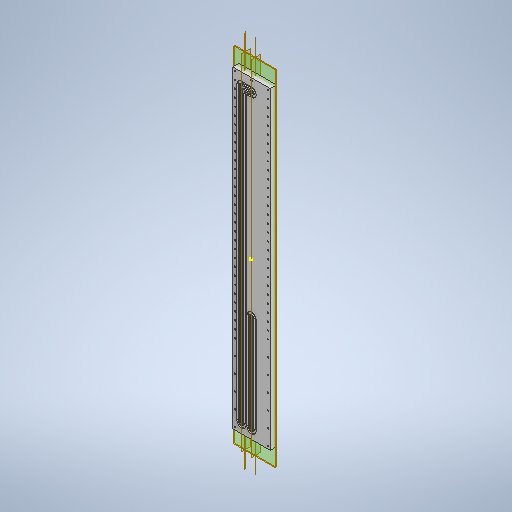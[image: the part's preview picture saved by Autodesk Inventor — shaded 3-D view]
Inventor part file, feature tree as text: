
AUTODESK INVENTOR PART (.ipt)
format: ipt  version: 2025 (Build 290162000, 162)  size: 955,904 bytes
history: native  units: mm
features: sketch x19, hole x11, other x10, extrude x8, pattern_linear x4, plane x4, fillet x1, projected_geometry x1
ambient origin geometry x8: Origin, YZ Plane, XZ Plane, XY Plane, X Axis, Y Axis, Z Axis, Center Point
bodies: Volumenkörper1 (feature_tree)
feature tree (58):
  sketch  "Skizze2"  dims[d3=22.5mm d4=5.0mm]
  sketch  "Skizze1"  dims[d0=90.0deg d1=5.0mm]
  extrude  "Extrusion1"  Depth=5.0mm
  extrude  "Extrusion2"  Depth=5.0mm
  extrude  "Extrusion4"  Depth=35.0mm
  hole  "Bohrung7"  [1 undecoded]
  sketch  "Skizze7"  dims[d14=35.0mm d15=5.0mm]
  hole  "Bohrung10"  [1 undecoded]
  hole  "Bohrung12"  [1 undecoded]
  pattern_linear  "Rechteckige Anordnung5"  Count1=50  [1 undecoded]
  sketch  "Skizze19"  dims[d24=250.0mm d26=10.0mm d27=0.0mm]
  extrude  "Extrusion8"  Depth=30.0mm
  sketch  "Skizze21"  dims[d28=1.6mm d29=0.0mm d68=2.0mm]
  extrude  "Extrusion9"  Depth=10.0mm TaperAngle=0.0deg
  extrude  "Extrusion10"  Depth=2.0mm
  other  "Arbeitsachse2"
  hole  "Bohrung13"  [1 undecoded]
  extrude  "Extrusion11"  TaperAngle=0.0deg  [1 undecoded]
  pattern_linear  "Rechteckige Anordnung6"  Count1=11 Spacing1=49.2mm
  hole  "Bohrung14"  [1 undecoded]
  other  "Arbeitsachse4"
  plane  "Arbeitsebene3"
  plane  "Arbeitsebene5"
  plane  "Arbeitsebene2"
  other  "Arbeitspunkt14"
  other  "Arbeitspunkt11"
  hole  "Bohrung15"  [1 undecoded]
  plane  "Arbeitsebene4"
  other  "Arbeitsachse7"
  other  "Arbeitspunkt13"
  other  "Arbeitspunkt12"
  hole  "Bohrung16"  [1 undecoded]
  sketch  "Skizze27"  dims[d122=4.0mm]
  extrude  "Extrusion12"  Depth=1.75mm
  fillet  "Rundung1"  Radius=4.5mm
  hole  "Bohrung19"  [1 undecoded]
  hole  "Bohrung20"  [1 undecoded]
  hole  "Bohrung Oberer Deckel"  [1 undecoded]
  pattern_linear  "Bohrungen Oberer Deckel"  Spacing1=1.9mm  [1 undecoded]
  hole  "Bohrung Zentrierplatte"  [1 undecoded]
  pattern_linear  "Bohrung Zentrierokatte"  Spacing1=3.5mm  [1 undecoded]
  sketch  "Skizze6"  dims[d5=90.0deg d13=35.0mm]
  sketch  "Skizze13"  dims[d16=90.0deg d17=5.0mm]
  sketch  "Skizze16"  dims[d18=90.0deg d19=45.0mm d21=500.0mm]
  sketch  "Skizze18"  dims[d22=60.0mm d23=30.0mm]
  sketch  "Skizze22"  dims[d76=14.0mm d78=1.9mm d79=0.0mm]
  sketch  "Skizze23"  dims[d83=2.0mm d85=0.0mm]
  sketch  "Skizze24"  dims[d86=90.0deg]
  sketch  "Skizze25"  dims[d91=2.0mm]
  other  "Arbeitsachse5"
  other  "Arbeitsachse6"
  sketch  "Skizze29"  dims[d145=2.0mm]
  projected_geometry  "Projizierte Kontur1"
  sketch  "Skizze30"  dims[d192=4.0mm d193=8.0mm d194=4.0mm d195=2.0mm d196=90.0deg d197=8.0mm d198=20.594885mm]
  sketch  "Skizze31"  dims[d224=4.0mm d225=6.0mm d226=5.5mm d227=4.0mm d228=90.0deg d229=5.0mm d230=20.594885mm]
  sketch  "Skizze32"  dims[d238=4.0mm]
  sketch  "Skizze33"  dims[d239=3.75mm d240=2.013mm d241=5.0mm d242=6.0mm d243=3.0mm d244=90.0deg d245=8.0mm d246=20.594885mm d247=110.0mm d249=49.2mm d250=20.0mm d252=52.5mm d253=3.75mm d254=3.75mm d255=3.75mm d256=1.75mm d258=4.5mm d259=4.5mm d260=3.55mm d271=2.0mm d272=1.9mm d273=0.0mm d274=1.5mm d275=3.5mm d276=1.75mm d277=1.75mm d280=1.9mm d281=0.0mm d283=1.9mm d284=0.0mm d285=225.0mm d286=450.0mm d287=10.0mm d288=144.1mm d289=30.0mm d290=0.0mm d292=3.55mm d295=3.75mm d296=20.0mm d297=4.0mm d298=6.0mm d299=3.023mm d300=2.0mm d301=14.3117mm d302=8.0mm d303=20.594885mm d304=18.0mm d305=18.0mm d306=2.0mm d307=2.0mm d308=2.0mm d309=2.0mm d310=8.4mm d312=9.0mm d313=5.6mm d314=0.0mm d315=100.0mm d317=30.0mm d318=10.0mm d319=10.0mm d320=4.0mm d321=6.0mm d322=4.0mm d323=2.0mm d324=90.0deg d325=5.0mm d326=20.594885mm d328=90.0deg d329=3.75mm d444=10.0mm d445=10.0mm d332=4.134mm d333=5.0mm d334=4.0mm d335=2.0mm d336=90.0deg d337=14.2mm d338=20.594885mm d341=90.0deg d442=10.0mm d443=10.0mm d344=4.134mm d345=5.0mm d346=4.0mm d347=2.0mm d348=90.0deg d349=14.2mm d350=20.594885mm d375=125.0mm d376=12.0mm d377=12.0mm d378=3.0mm d379=0.0mm d380=2.0mm d382=1.75mm d384=1.75mm d385=7.3mm d386=7.3mm d387=3.75mm d388=30.0mm d389=3.0mm d390=6.0mm d391=4.0mm d392=2.0mm d393=90.0deg d394=8.0mm d395=20.594885mm d396=360.7mm d397=3.75mm d398=3.0mm d399=6.0mm d400=4.0mm d401=2.0mm d402=90.0deg d403=8.0mm d404=20.594885mm d409=16.3mm d410=3.75mm d411=2.459mm d412=6.0mm d413=4.0mm d414=2.0mm d415=90.0deg d416=8.0mm d417=20.594885mm d418=140.0mm d420=24.6mm d421=20.0mm d423=52.5mm d424=28.6mm d425=3.75mm d426=2.459mm d427=6.0mm d428=4.0mm d429=2.0mm d430=90.0deg d431=8.0mm d432=20.594885mm d433=100.0mm d435=49.2mm d436=20.0mm d438=52.5mm d439=1.5mm d190=1.0mm d191=1.0mm d199=0.0625mm d200=0.75mm d201=0.375mm d327=0.0625mm d366=1.0mm d367=1.0mm d368=1.0mm d369=0.15mm d370=0.25mm d371=0.375mm d372=14.3117mm d373=0.75mm d374=20.594885mm d419=0.75mm d440=1.0mm d441=1.0mm d446=1.0mm d447=0.15mm d448=0.25mm d449=0.375mm d450=14.3117mm d451=0.75mm d452=20.594885mm d453=0.0625mm d454=0.75mm d455=0.375mm]
  other  "Arbeitsachse8"
note: 15 required parameter values undecoded (feature->parameter linkage not recoverable at this tier; creation-order binding heuristic only, values carry confidence <= 0.55)
